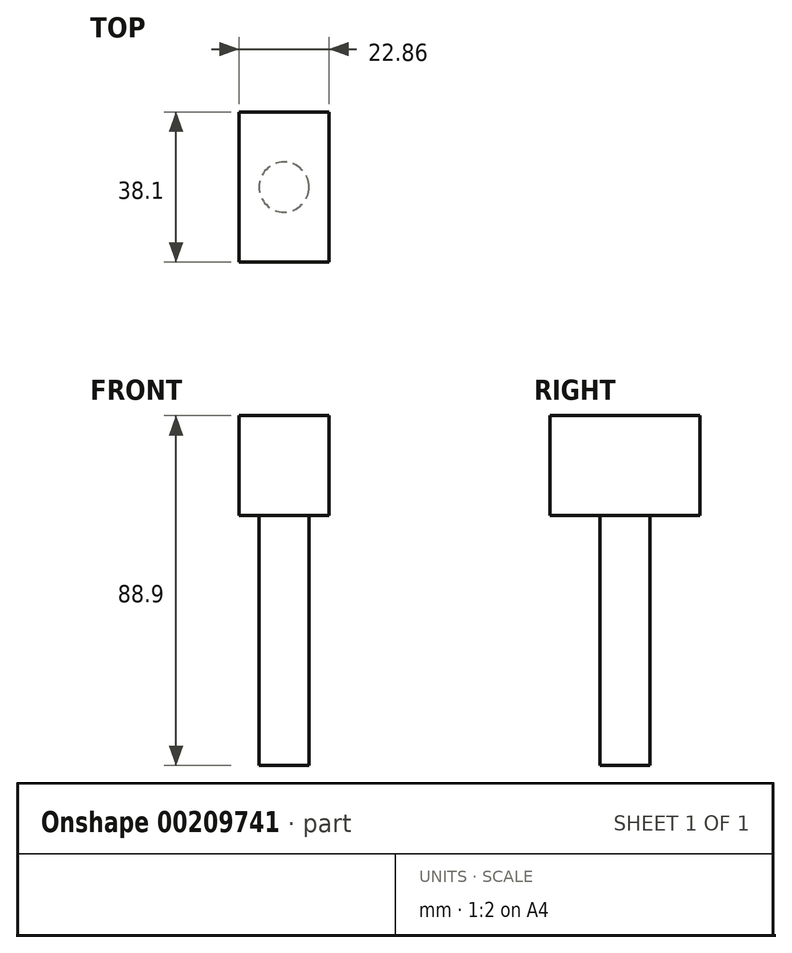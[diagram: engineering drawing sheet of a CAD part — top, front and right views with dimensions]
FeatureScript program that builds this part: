
annotation { "Feature Type Name" : "Feature", "Feature Type Description" : "" }
export const myFeature = defineFeature(function(context is Context, id is Id, definition is map)
    precondition{}
    {
        {
            var Q0;
            Q0=qCreatedBy(makeId("Front.planeOp"),FACE);
            var sketch = newSketch(context, id + "F0", { "sketchPlane" : qUnion([Q0])});
            skLineSegment(sketch, "E0.bottom", {"start": v(0, 0) * mm, "end": v(6.35, 0) * mm});
            skLineSegment(sketch, "E0.top", {"start": v(0, 63.5) * mm, "end": v(6.35, 63.5) * mm});
            skLineSegment(sketch, "E0.left", {"start": v(0, 0) * mm, "end": v(0, 63.5) * mm});
            skLineSegment(sketch, "E0.right", {"start": v(6.35, 0) * mm, "end": v(6.35, 63.5) * mm});
            skSolve(sketch);
        }
        {
            var Q0;
            Q0=makeQuery(id+"F0.imprint","IMPRINT",FACE,{"disambiguationData":[TD([[makeQuery(id+"F0.imprint","IMPRINT",EDGE,{"derivedFrom":sQuery(id+"F0.wireOp",EDGE,"E0.bottom")}),1.0]])]});
            var Q1;
            Q1=sQuery(id+"F0.wireOp",EDGE,"E0.left");
            revolve(context, id + "F1", {"entities" : qUnion([Q0]), "axis" : qUnion([Q1]), "revolveType" : RevolveType.FULL});
        }
        {
            var Q0;
            Q0=makeQuery(id+"F1.opRevolve","SWEPT_FACE",FACE,{"disambiguationData":[OSD([sQuery(id+"F0.wireOp",EDGE,"E0.top")])]});
            var sketch = newSketch(context, id + "F2", { "sketchPlane" : qUnion([Q0])});
            skLineSegment(sketch, "E1.bottom", {"start": v(11.43, 19.05) * mm, "end": v(-11.43, 19.05) * mm});
            skLineSegment(sketch, "E1.top", {"start": v(11.43, -19.05) * mm, "end": v(-11.43, -19.05) * mm});
            skLineSegment(sketch, "E1.left", {"start": v(11.43, 19.05) * mm, "end": v(11.43, -19.05) * mm});
            skLineSegment(sketch, "E1.right", {"start": v(-11.43, 19.05) * mm, "end": v(-11.43, -19.05) * mm});
            skPoint(sketch, "E1.middle", {"position": v(0, 0) * mm});
            skSolve(sketch);
        }
        {
            var Q0;
            Q0 = qSketchRegion(id + "F2", true);
            extrude(context, id + "F3", {"entities" : qUnion([Q0]), "operationType" : NewBodyOperationType.ADD, "depth" : 25.4 * mm});
        }
    });
